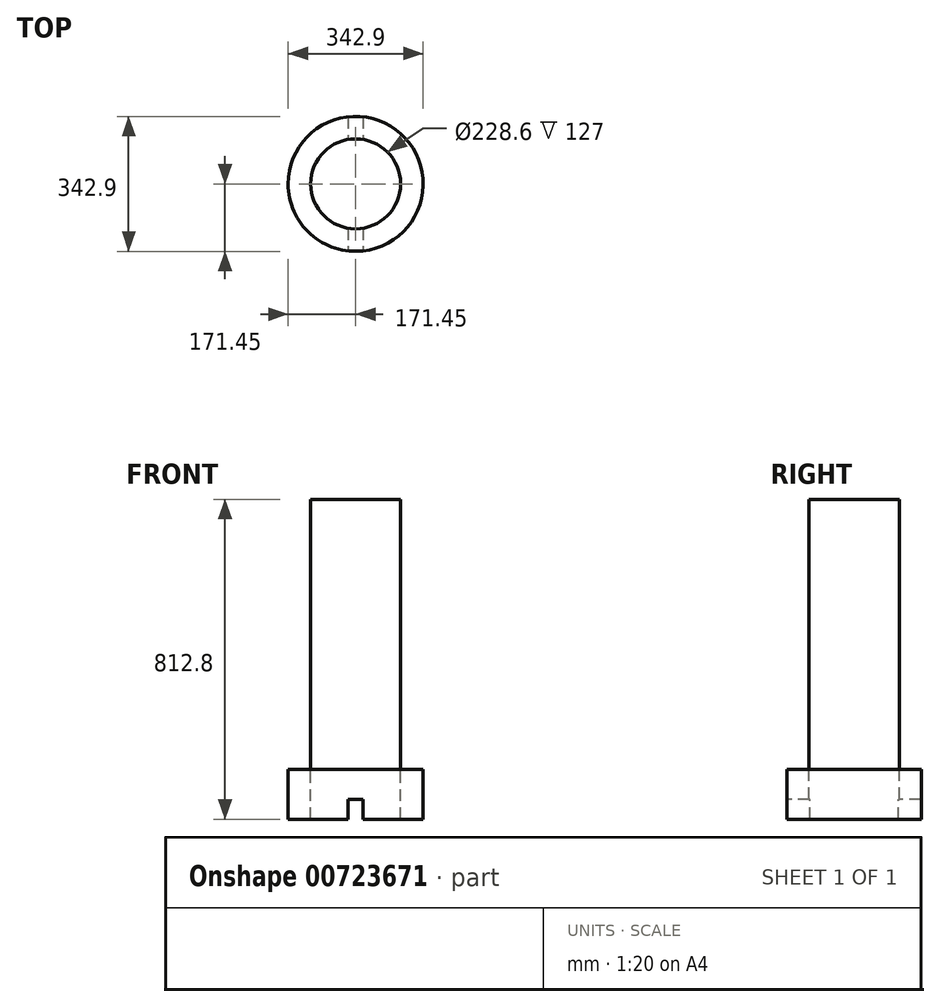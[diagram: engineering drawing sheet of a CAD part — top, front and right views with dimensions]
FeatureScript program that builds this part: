
annotation { "Feature Type Name" : "Feature", "Feature Type Description" : "" }
export const myFeature = defineFeature(function(context is Context, id is Id, definition is map)
    precondition{}
    {
        {
            var Q0;
            Q0=qCreatedBy(makeId("Top.planeOp"),FACE);
            var sketch = newSketch(context, id + "F0", { "sketchPlane" : qUnion([Q0])});
            skCircle(sketch, "E0", {"center": v(0, 0) * mm, "radius": 114.3 * mm});
            skSolve(sketch);
        }
        {
            var Q0;
            Q0 = qSketchRegion(id + "F0", true);
            extrude(context, id + "F1", {"entities" : qUnion([Q0]), "depth" : 685.8 * mm, "offsetDistance" : 25.4 * mm});
        }
        {
            var Q0;
            Q0=makeQuery(id+"F1.opExtrude","CAP_FACE",FACE,{"disambiguationData":[OSD([sQuery(id+"F0.wireOp",EDGE,"E0")])],"isStart":true});
            var sketch = newSketch(context, id + "F2", { "sketchPlane" : qUnion([Q0])});
            skCircle(sketch, "E1", {"center": v(0, 0) * mm, "radius": 171.45 * mm});
            skSolve(sketch);
        }
        {
            var Q0;
            Q0=makeQuery(id+"F2.imprint","IMPRINT",FACE,{"disambiguationData":[TD([[makeQuery(id+"F2.imprint","IMPRINT",EDGE,{"derivedFrom":sQuery(id+"F2.wireOp",EDGE,"E1")}),1.0]])]});
            extrude(context, id + "F3", {"entities" : qUnion([Q0]), "depth" : 127 * mm, "offsetDistance" : 25.4 * mm});
        }
        {
            var Q0;
            Q0=qCreatedBy(makeId("Front.planeOp"),FACE);
            var sketch = newSketch(context, id + "F4", { "sketchPlane" : qUnion([Q0])});
            skLineSegment(sketch, "E2.bottom", {"start": v(-19.05, -127) * mm, "end": v(19.05, -127) * mm});
            skLineSegment(sketch, "E2.top", {"start": v(-19.05, -76.2) * mm, "end": v(19.05, -76.2) * mm});
            skLineSegment(sketch, "E2.left", {"start": v(-19.05, -127) * mm, "end": v(-19.05, -76.2) * mm});
            skLineSegment(sketch, "E2.right", {"start": v(19.05, -127) * mm, "end": v(19.05, -76.2) * mm});
            skSolve(sketch);
        }
        {
            var Q0;
            Q0 = qSketchRegion(id + "F4", true);
            extrude(context, id + "F5", {"entities" : qUnion([Q0]), "operationType" : NewBodyOperationType.REMOVE, "endBound" : BoundingType.SYMMETRIC, "oppositeDirection" : true, "depth" : 452.12 * mm, "offsetDistance" : 25.4 * mm});
        }
    });
